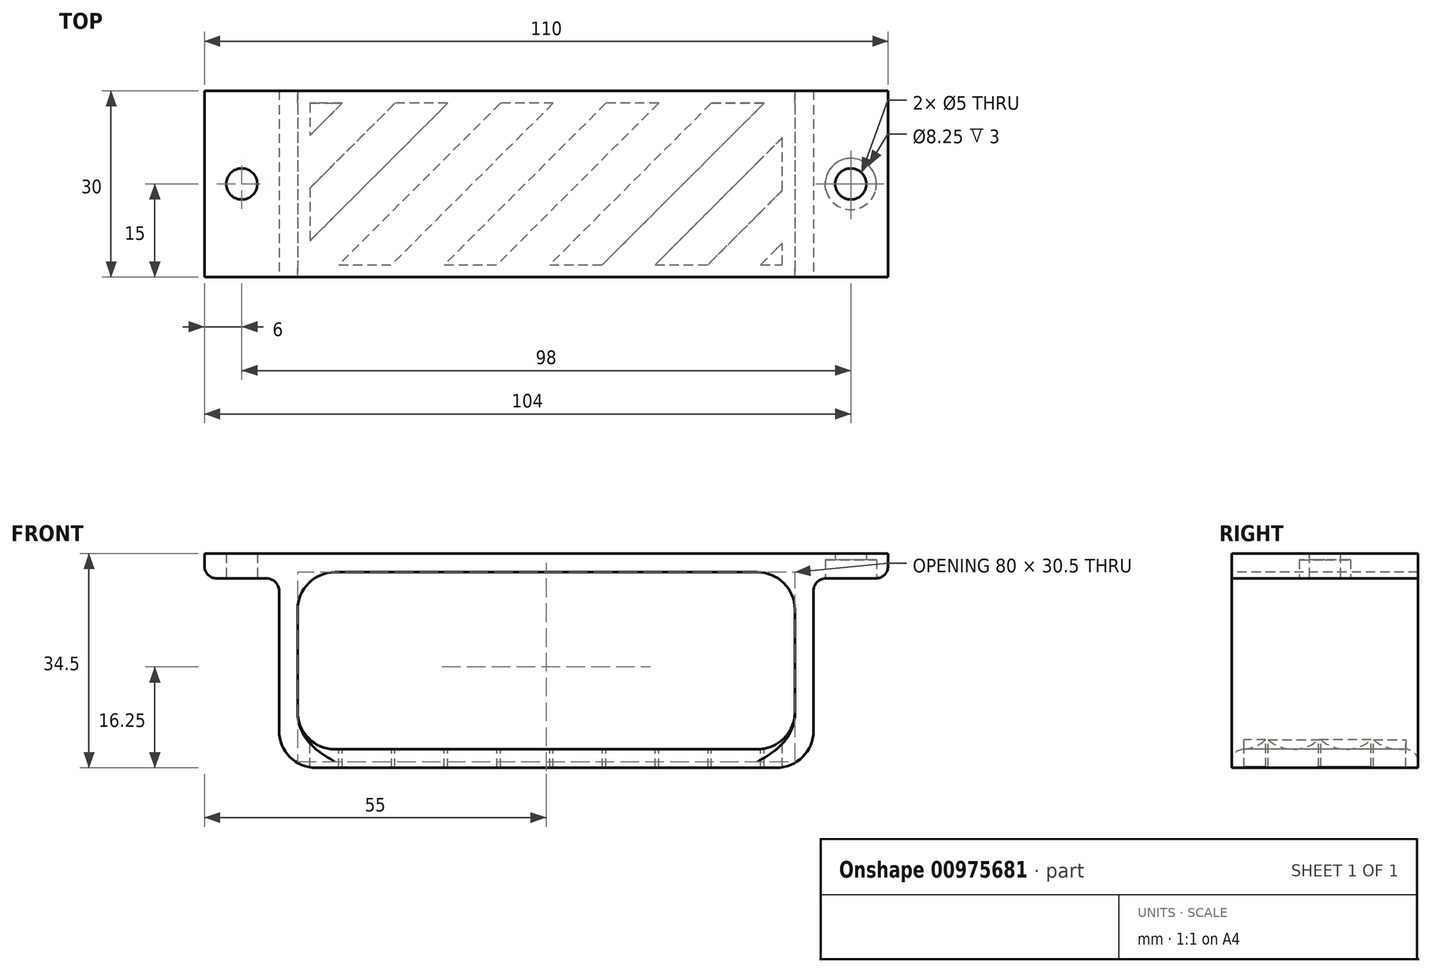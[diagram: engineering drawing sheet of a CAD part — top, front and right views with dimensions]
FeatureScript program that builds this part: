
annotation { "Feature Type Name" : "Feature", "Feature Type Description" : "" }
export const myFeature = defineFeature(function(context is Context, id is Id, definition is map)
    precondition{}
    {
        {
            var Q0;
            Q0=qCreatedBy(makeId("Front.planeOp"),FACE);
            var sketch = newSketch(context, id + "F0", { "sketchPlane" : qUnion([Q0])});
            skLineSegment(sketch, "E0.bottom", {"start": v(-43, 17.25) * mm, "end": v(43, 17.25) * mm});
            skLineSegment(sketch, "E0.top", {"start": v(-43, -17.25) * mm, "end": v(43, -17.25) * mm});
            skLineSegment(sketch, "E0.left", {"start": v(-43, 17.25) * mm, "end": v(-43, -17.25) * mm});
            skLineSegment(sketch, "E0.right", {"start": v(43, 17.25) * mm, "end": v(43, -17.25) * mm});
            skLineSegment(sketch, "E1.bottom", {"start": v(-40, 14.25) * mm, "end": v(40, 14.25) * mm});
            skLineSegment(sketch, "E1.top", {"start": v(-40, -14.25) * mm, "end": v(40, -14.25) * mm});
            skLineSegment(sketch, "E1.left", {"start": v(-40, 14.25) * mm, "end": v(-40, -14.25) * mm});
            skLineSegment(sketch, "E1.right", {"start": v(40, 14.25) * mm, "end": v(40, -14.25) * mm});
            skLineSegment(sketch, "E2.bottom", {"start": v(43, 17.25) * mm, "end": v(55, 17.25) * mm});
            skLineSegment(sketch, "E2.top", {"start": v(43, 13.25) * mm, "end": v(55, 13.25) * mm});
            skLineSegment(sketch, "E2.left", {"start": v(43, 17.25) * mm, "end": v(43, 13.25) * mm});
            skLineSegment(sketch, "E2.right", {"start": v(55, 17.25) * mm, "end": v(55, 13.25) * mm});
            skPoint(sketch, "E3", {"position": v(0, 17.25) * mm});
            skLineSegment(sketch, "E4", {"start": v(0, 44.97) * mm, "end": v(0, -38.57) * mm, "construction": true});
            skLineSegment(sketch, "E5.MirrorCS", {"start": v(-43, 17.25) * mm, "end": v(-55, 17.25) * mm});
            skLineSegment(sketch, "E6.MirrorCS", {"start": v(-55, 17.25) * mm, "end": v(-55, 13.25) * mm});
            skLineSegment(sketch, "E7.MirrorCS", {"start": v(-43, 13.25) * mm, "end": v(-55, 13.25) * mm});
            skLineSegment(sketch, "E8", {"start": v(-40, 0) * mm, "end": v(40, 0) * mm, "construction": true});
            skPoint(sketch, "E9", {"position": v(0, 0) * mm});
            skSolve(sketch);
        }
        {
            var Q0;
            Q0=qCreatedBy(makeId("Top.planeOp"),FACE);
            var sketch = newSketch(context, id + "F1", { "sketchPlane" : qUnion([Q0])});
            skLineSegment(sketch, "E10.0", {"start": v(38, 28) * mm, "end": v(38, 2) * mm});
            skLineSegment(sketch, "E10.1", {"start": v(38, 28) * mm, "end": v(-38, 28) * mm});
            skLineSegment(sketch, "E10.2", {"start": v(-38, 28) * mm, "end": v(-38, 2) * mm});
            skLineSegment(sketch, "E10.3", {"start": v(-38, 2) * mm, "end": v(38, 2) * mm});
            skLineSegment(sketch, "E11", {"start": v(34.5, 2) * mm, "end": v(38, 5.5) * mm});
            skLineSegment(sketch, "E12.0", {"start": v(26.01, 2) * mm, "end": v(38, 13.99) * mm});
            skLineSegment(sketch, "E13.0", {"start": v(17.53, 2) * mm, "end": v(38, 22.47) * mm});
            skLineSegment(sketch, "E14.0", {"start": v(9.04, 2) * mm, "end": v(35.04, 28) * mm});
            skLineSegment(sketch, "E15.0", {"start": v(0.56, 2) * mm, "end": v(26.56, 28) * mm});
            skLineSegment(sketch, "E16.0", {"start": v(-7.93, 2) * mm, "end": v(18.07, 28) * mm});
            skLineSegment(sketch, "E17.0", {"start": v(-16.41, 2) * mm, "end": v(9.59, 28) * mm});
            skLineSegment(sketch, "E18.0", {"start": v(-24.9, 2) * mm, "end": v(1.1, 28) * mm});
            skLineSegment(sketch, "E19.0", {"start": v(-33.38, 2) * mm, "end": v(-7.38, 28) * mm});
            skLineSegment(sketch, "E20.0", {"start": v(-38, 5.87) * mm, "end": v(-15.87, 28) * mm});
            skLineSegment(sketch, "E21.0", {"start": v(-38, 14.35) * mm, "end": v(-24.35, 28) * mm});
            skLineSegment(sketch, "E22.0", {"start": v(-38, 22.84) * mm, "end": v(-32.84, 28) * mm});
            skLineSegment(sketch, "E23", {"start": v(-47.7, 2) * mm, "end": v(-12.13, 2) * mm, "construction": true});
            skPoint(sketch, "E24", {"position": v(-38, 2) * mm});
            skLineSegment(sketch, "E25.0", {"start": v(-50, 30) * mm, "end": v(-50, 0) * mm, "construction": true});
            skPoint(sketch, "E26.0.end.orphan", {"position": v(-43, 32) * mm});
            skLineSegment(sketch, "E27.0", {"start": v(-42, 30) * mm, "end": v(-42, 0) * mm, "construction": true});
            skLineSegment(sketch, "E28.0", {"start": v(42, 30) * mm, "end": v(42, 0) * mm, "construction": true});
            skSolve(sketch);
        }
        {
            var Q0;
            Q0=makeQuery(id+"F0.imprint","IMPRINT",FACE,{"disambiguationData":[TD([[makeQuery(id+"F0.imprint","IMPRINT",EDGE,{"derivedFrom":sQuery(id+"F0.wireOp",EDGE,"E0.bottom")}),-1.0]])]});
            var Q1;
            Q1=makeQuery(id+"F0.imprint","IMPRINT",FACE,{"disambiguationData":[TD([[makeQuery(id+"F0.imprint","IMPRINT",EDGE,{"derivedFrom":sQuery(id+"F0.wireOp",EDGE,"E2.bottom")}),-1.0]])]});
            var Q2;
            {var subQ0=sQuery(id+"F0.wireOp",EDGE,"E5.MirrorCS");Q2=makeQuery(id+"F0.imprint","IMPRINT",FACE,{"disambiguationData":[TD([[makeQuery(id+"F0.imprint","IMPRINT",EDGE,{"derivedFrom":subQ0}),1.0]])]});}
            extrude(context, id + "F2", {"entities" : qUnion([Q0, Q1, Q2]), "oppositeDirection" : true, "depth" : 30 * mm, "offsetDistance" : 25 * mm});
        }
        {
            var Q0;
            Q0=makeQuery(id+"F2.opExtrude","CAP_EDGE",EDGE,{"disambiguationData":[OSD([sQuery(id+"F0.wireOp",EDGE,"E1.top")])],"isStart":true});
            var Q1;
            Q1=makeQuery(id+"F2.opExtrude","CAP_EDGE",EDGE,{"disambiguationData":[OSD([sQuery(id+"F0.wireOp",EDGE,"E1.top")])],"isStart":false});
            var Q2;
            Q2=makeQuery(id+"FBCRjVHo6mlkU5s_1.opExtrude","SWEPT_EDGE",EDGE,{"disambiguationData":[OSD([sQuery(id+"FKhxplyHhKLiEK4_0.wireOp",EDGE,"db78b1f0-e7e6-4282-9ba8-f3fa515991c4.0"),sQuery(id+"FKhxplyHhKLiEK4_0.wireOp",EDGE,"FEgogpPj-nWPP-g54Q-uAWN-uniVl4YHIuRG")])]});
            var Q3;
            Q3=makeQuery(id+"FBCRjVHo6mlkU5s_1.opExtrude","CAP_EDGE",EDGE,{"disambiguationData":[OSD([sQuery(id+"FKhxplyHhKLiEK4_0.wireOp",EDGE,"db78b1f0-e7e6-4282-9ba8-f3fa515991c4.0")])],"isStart":true});
            var Q4;
            Q4=makeQuery(id+"FBCRjVHo6mlkU5s_1.opExtrude","CAP_EDGE",EDGE,{"disambiguationData":[OSD([sQuery(id+"FKhxplyHhKLiEK4_0.wireOp",EDGE,"db78b1f0-e7e6-4282-9ba8-f3fa515991c4.0")])],"isStart":false});
            var Q5;
            Q5=makeQuery(id+"FBCRjVHo6mlkU5s_1.opExtrude","SWEPT_EDGE",EDGE,{"disambiguationData":[OSD([sQuery(id+"FKhxplyHhKLiEK4_0.wireOp",EDGE,"D6vk4sKK-LBSh-OOkH-Cg5b-jT46tOwvnKm1"),sQuery(id+"FKhxplyHhKLiEK4_0.wireOp",EDGE,"db78b1f0-e7e6-4282-9ba8-f3fa515991c4.0")])]});
            fillet(context, id + "F3", {"entities" : qUnion([Q0, Q1, Q2, Q3, Q4, Q5]), "radius" : 2 * mm, "tangentPropagation" : true, "allowEdgeOverflow" : false});
        }
        {
            var Q0;
            Q0=qCreatedBy(makeId("Top.planeOp"),FACE);
            var sketch = newSketch(context, id + "F4", { "sketchPlane" : qUnion([Q0])});
            skCircle(sketch, "E29", {"center": v(49, 15) * mm, "radius": 2.5 * mm});
            skCircle(sketch, "E30.MirrorC", {"center": v(-49, 15) * mm, "radius": 4.12 * mm});
            skPoint(sketch, "E31.0", {"position": v(-47, 60) * mm});
            skPoint(sketch, "E32.0", {"position": v(-49, 0) * mm});
            skPoint(sketch, "E33.0", {"position": v(49, 0) * mm});
            skPoint(sketch, "E34", {"position": v(49, 30) * mm});
            skLineSegment(sketch, "E35.0", {"start": v(-43, 30) * mm, "end": v(-55, 30) * mm, "construction": true});
            skLineSegment(sketch, "E36", {"start": v(-49, 0) * mm, "end": v(-49, 30) * mm, "construction": true});
            skLineSegment(sketch, "E37", {"start": v(49, 0) * mm, "end": v(49, 30) * mm, "construction": true});
            skCircle(sketch, "E38", {"center": v(-49, 15) * mm, "radius": 2.5 * mm});
            skCircle(sketch, "E39", {"center": v(49, 15) * mm, "radius": 4.12 * mm});
            skSolve(sketch);
        }
        {
            var Q0;
            Q0=makeQuery(id+"F4.imprint","IMPRINT",FACE,{"disambiguationData":[TD([[makeQuery(id+"F4.imprint","IMPRINT",EDGE,{"derivedFrom":sQuery(id+"F4.wireOp",EDGE,"E29")}),1.0]])]});
            var Q1;
            Q1=makeQuery(id+"F4.imprint","IMPRINT",FACE,{"disambiguationData":[TD([[makeQuery(id+"F4.imprint","IMPRINT",EDGE,{"derivedFrom":sQuery(id+"F4.wireOp",EDGE,"E38")}),1.0]])]});
            var Q2;
            Q2=makeQuery(id+"F2.opExtrude","SWEPT_FACE",FACE,{"disambiguationData":[OSD([sQuery(id+"F0.wireOp",EDGE,"E0.bottom"),sQuery(id+"F0.wireOp",EDGE,"E2.bottom"),sQuery(id+"F0.wireOp",EDGE,"E5.MirrorCS")])]});
            extrude(context, id + "F5", {"entities" : qUnion([Q0, Q1]), "operationType" : NewBodyOperationType.REMOVE, "endBound" : BoundingType.UP_TO_SURFACE, "depth" : 4 * mm, "endBoundEntityFace" : qUnion([Q2]), "offsetDistance" : 25 * mm});
        }
        {
            var Q0;
            Q0=makeQuery(id+"F2.opExtrude","SWEPT_EDGE",EDGE,{"disambiguationData":[OSD([sQuery(id+"F0.wireOp",EDGE,"E1.bottom"),sQuery(id+"F0.wireOp",EDGE,"E1.left")])]});
            var Q1;
            Q1=makeQuery(id+"F2.opExtrude","SWEPT_EDGE",EDGE,{"disambiguationData":[OSD([sQuery(id+"F0.wireOp",EDGE,"E1.top"),sQuery(id+"F0.wireOp",EDGE,"E1.left")])]});
            var Q2;
            Q2=makeQuery(id+"F2.opExtrude","SWEPT_EDGE",EDGE,{"disambiguationData":[OSD([sQuery(id+"F0.wireOp",EDGE,"E1.bottom"),sQuery(id+"F0.wireOp",EDGE,"E1.right")])]});
            var Q3;
            Q3=makeQuery(id+"F2.opExtrude","SWEPT_EDGE",EDGE,{"disambiguationData":[OSD([sQuery(id+"F0.wireOp",EDGE,"E1.top"),sQuery(id+"F0.wireOp",EDGE,"E1.right")])]});
            var Q4;
            Q4=makeQuery(id+"F2.opExtrude","SWEPT_EDGE",EDGE,{"disambiguationData":[OSD([sQuery(id+"F0.wireOp",EDGE,"E0.top"),sQuery(id+"F0.wireOp",EDGE,"E0.left")])]});
            var Q5;
            Q5=makeQuery(id+"F2.opExtrude","SWEPT_EDGE",EDGE,{"disambiguationData":[OSD([sQuery(id+"F0.wireOp",EDGE,"E0.top"),sQuery(id+"F0.wireOp",EDGE,"E0.right")])]});
            fillet(context, id + "F6", {"entities" : qUnion([Q0, Q1, Q2, Q3, Q4, Q5]), "radius" : 6 * mm, "tangentPropagation" : true, "defaultsChanged" : false, "vertexSettings" : [], "allowEdgeOverflow" : false});
        }
        {
            var Q0;
            Q0=makeQuery(id+"F2.opExtrude","SWEPT_EDGE",EDGE,{"disambiguationData":[OSD([sQuery(id+"F0.wireOp",EDGE,"E6.MirrorCS"),sQuery(id+"F0.wireOp",EDGE,"E7.MirrorCS")])]});
            var Q1;
            Q1=makeQuery(id+"F2.opExtrude","SWEPT_EDGE",EDGE,{"disambiguationData":[OSD([sQuery(id+"F0.wireOp",EDGE,"E2.top"),sQuery(id+"F0.wireOp",EDGE,"E2.right")])]});
            var Q2;
            Q2=makeQuery(id+"F2.opExtrude","SWEPT_EDGE",EDGE,{"disambiguationData":[OSD([sQuery(id+"F0.wireOp",EDGE,"E0.right"),sQuery(id+"F0.wireOp",EDGE,"E2.top"),sQuery(id+"F0.wireOp",EDGE,"E2.left")])]});
            var Q3;
            Q3=makeQuery(id+"F2.opExtrude","SWEPT_EDGE",EDGE,{"disambiguationData":[OSD([sQuery(id+"F0.wireOp",EDGE,"E0.left"),sQuery(id+"F0.wireOp",EDGE,"E7.MirrorCS")])]});
            fillet(context, id + "F7", {"entities" : qUnion([Q0, Q1, Q2, Q3]), "tangentPropagation" : true, "radius" : 2 * mm, "defaultsChanged" : false, "vertexSettings" : [], "allowEdgeOverflow" : false});
        }
        {
            var Q0;
            {var subQ3=sQuery(id+"F1.wireOp",EDGE,"E11");Q0=makeQuery(id+"F1.imprint","IMPRINT",FACE,{"disambiguationData":[TD([[makeQuery(id+"F1.imprint","IMPRINT",EDGE,{"derivedFrom":subQ3}),-1.0]])]});}
            var Q1;
            {var subQ0=sQuery(id+"F1.wireOp",EDGE,"E12.0");Q1=makeQuery(id+"F1.imprint","IMPRINT",FACE,{"disambiguationData":[TD([[makeQuery(id+"F1.imprint","IMPRINT",EDGE,{"derivedFrom":subQ0}),1.0]])]});}
            var Q2;
            {var subQ0=sQuery(id+"F1.wireOp",EDGE,"E14.0");Q2=makeQuery(id+"F1.imprint","IMPRINT",FACE,{"disambiguationData":[TD([[makeQuery(id+"F1.imprint","IMPRINT",EDGE,{"derivedFrom":subQ0}),1.0]])]});}
            var Q3;
            {var subQ0=sQuery(id+"F1.wireOp",EDGE,"E16.0");Q3=makeQuery(id+"F1.imprint","IMPRINT",FACE,{"disambiguationData":[TD([[makeQuery(id+"F1.imprint","IMPRINT",EDGE,{"derivedFrom":subQ0}),1.0]])]});}
            var Q4;
            {var subQ0=sQuery(id+"F1.wireOp",EDGE,"E18.0");Q4=makeQuery(id+"F1.imprint","IMPRINT",FACE,{"disambiguationData":[TD([[makeQuery(id+"F1.imprint","IMPRINT",EDGE,{"derivedFrom":subQ0}),1.0]])]});}
            var Q5;
            {var subQ0=sQuery(id+"F1.wireOp",EDGE,"E20.0");Q5=makeQuery(id+"F1.imprint","IMPRINT",FACE,{"disambiguationData":[TD([[makeQuery(id+"F1.imprint","IMPRINT",EDGE,{"derivedFrom":subQ0}),1.0]])]});}
            var Q6;
            {var subQ3=sQuery(id+"F1.wireOp",EDGE,"E22.0");Q6=makeQuery(id+"F1.imprint","IMPRINT",FACE,{"disambiguationData":[TD([[makeQuery(id+"F1.imprint","IMPRINT",EDGE,{"derivedFrom":subQ3}),1.0]])]});}
            var Q7;
            Q7=makeQuery(id+"F2.opExtrude","SWEPT_FACE",FACE,{"disambiguationData":[OSD([sQuery(id+"F0.wireOp",EDGE,"E0.top")])]});
            extrude(context, id + "F8", {"entities" : qUnion([Q0, Q1, Q2, Q3, Q4, Q5, Q6]), "operationType" : NewBodyOperationType.REMOVE, "endBound" : BoundingType.UP_TO_SURFACE, "oppositeDirection" : true, "depth" : 25 * mm, "endBoundEntityFace" : qUnion([Q7]), "offsetDistance" : 25 * mm});
        }
        {
            var Q0;
            Q0=makeQuery(id+"F4.imprint","IMPRINT",FACE,{"disambiguationData":[TD([[makeQuery(id+"F4.imprint","IMPRINT",EDGE,{"derivedFrom":sQuery(id+"F4.wireOp",EDGE,"E30.MirrorC")}),-1.0]])]});
            var Q1;
            Q1=makeQuery(id+"F4.imprint","IMPRINT",FACE,{"disambiguationData":[TD([[makeQuery(id+"F4.imprint","IMPRINT",EDGE,{"derivedFrom":sQuery(id+"F4.wireOp",EDGE,"E29")}),-1.0]])]});
            extrude(context, id + "F9", {"entities" : qUnion([Q0, Q1]), "operationType" : NewBodyOperationType.REMOVE, "depth" : 16.25 * mm, "offsetDistance" : 25 * mm});
        }
    });
